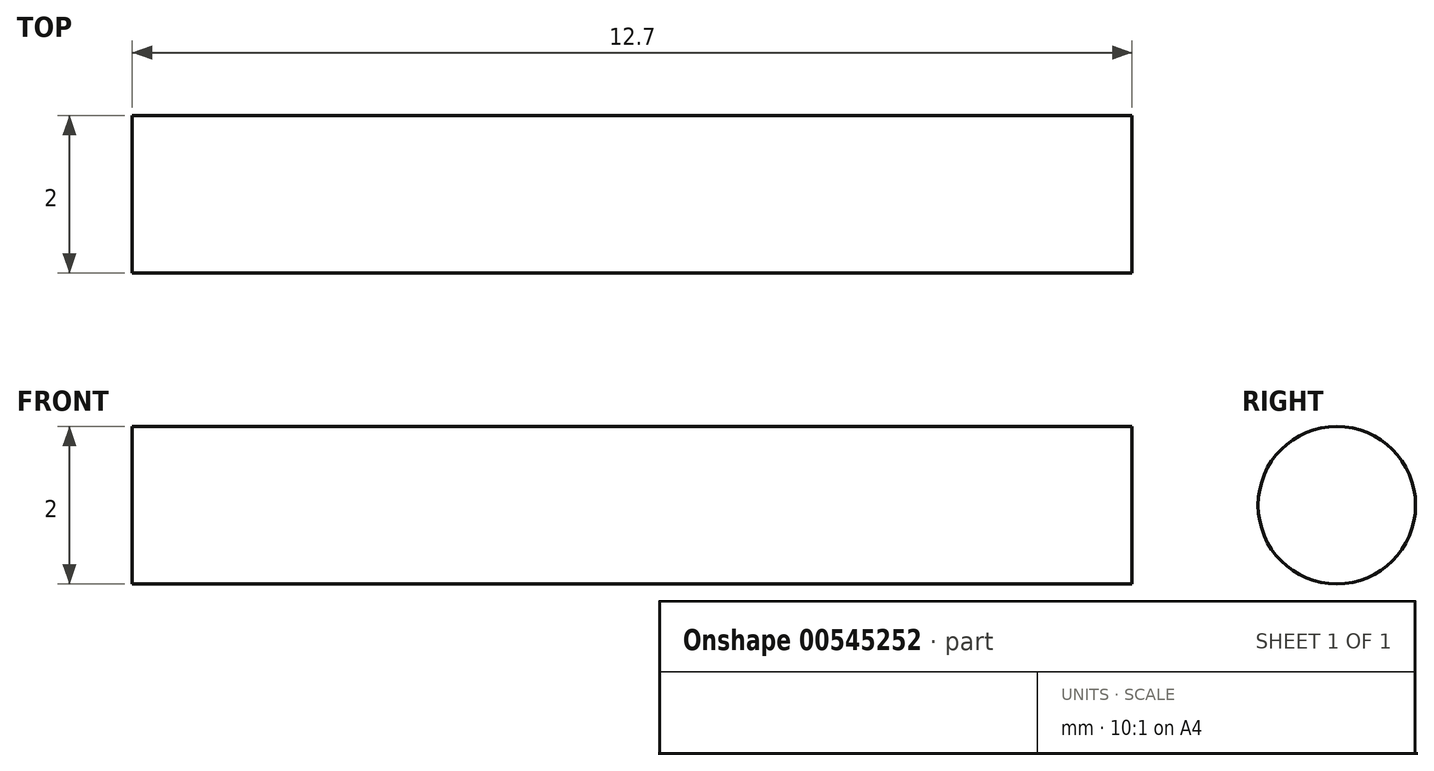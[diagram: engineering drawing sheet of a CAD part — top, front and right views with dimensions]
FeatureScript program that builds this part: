
annotation { "Feature Type Name" : "Feature", "Feature Type Description" : "" }
export const myFeature = defineFeature(function(context is Context, id is Id, definition is map)
    precondition{}
    {
        {
            var Q0;
            Q0=qCreatedBy(makeId("Right.planeOp"),FACE);
            var sketch = newSketch(context, id + "F0", { "sketchPlane" : qUnion([Q0])});
            skCircle(sketch, "E0", {"center": v(0, 0) * mm, "radius": 1 * mm});
            skSolve(sketch);
        }
        {
            var Q0;
            Q0 = qSketchRegion(id + "F0", true);
            extrude(context, id + "F1", {"entities" : qUnion([Q0]), "depth" : 12.7 * mm, "offsetDistance" : 25.4 * mm});
        }
    });
